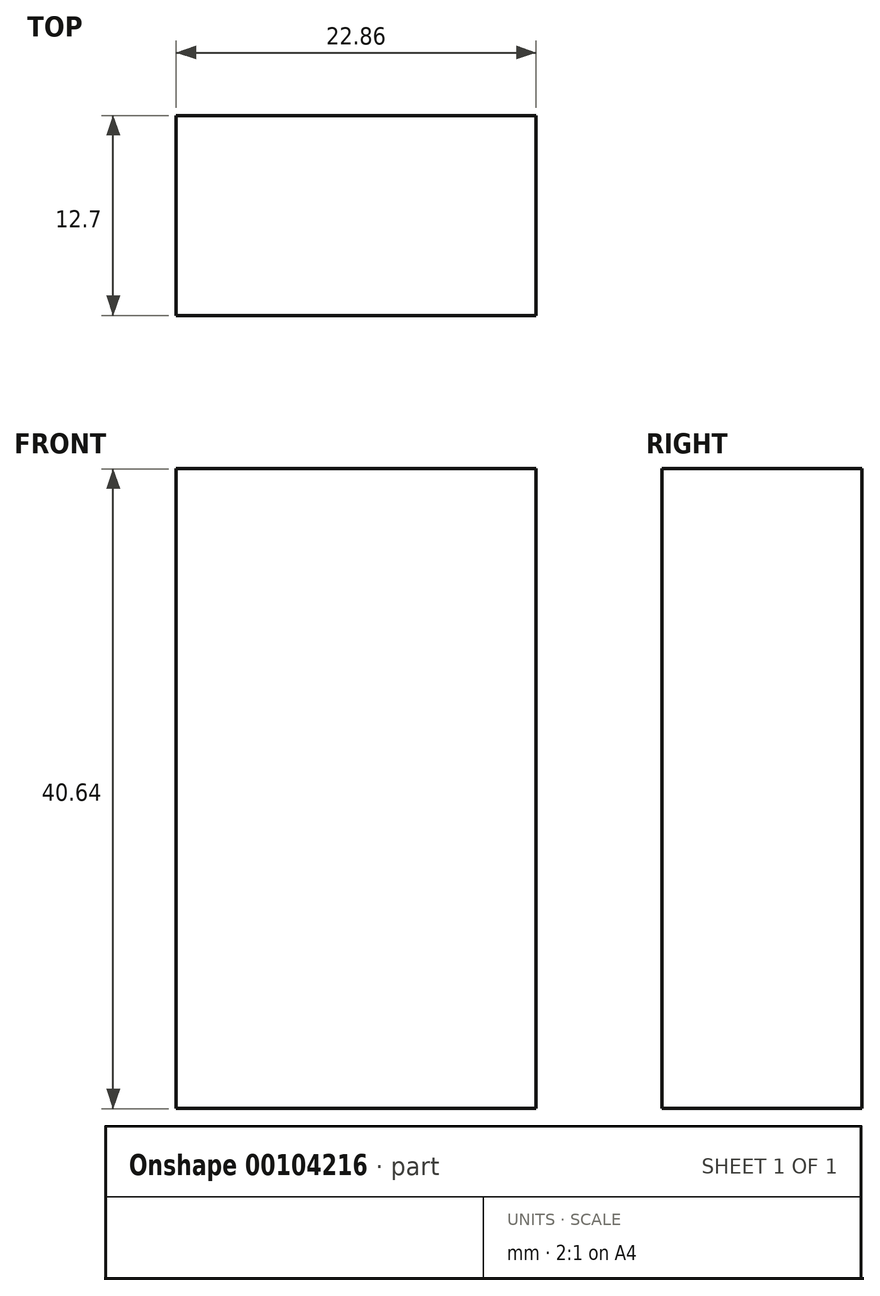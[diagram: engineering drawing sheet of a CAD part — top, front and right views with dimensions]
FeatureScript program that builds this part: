
annotation { "Feature Type Name" : "Feature", "Feature Type Description" : "" }
export const myFeature = defineFeature(function(context is Context, id is Id, definition is map)
    precondition{}
    {
        {
            var Q0;
            Q0=qCreatedBy(makeId("Front.planeOp"),FACE);
            var sketch = newSketch(context, id + "F0", { "sketchPlane" : qUnion([Q0])});
            skLineSegment(sketch, "E0.bottom", {"start": v(-20.82, -10.24) * mm, "end": v(2.04, -10.24) * mm});
            skLineSegment(sketch, "E0.top", {"start": v(-20.82, 30.4) * mm, "end": v(2.04, 30.4) * mm});
            skLineSegment(sketch, "E0.left", {"start": v(-20.82, -10.24) * mm, "end": v(-20.82, 30.4) * mm});
            skLineSegment(sketch, "E0.right", {"start": v(2.04, -10.24) * mm, "end": v(2.04, 30.4) * mm});
            skSolve(sketch);
        }
        {
            var Q0;
            Q0=makeQuery(id+"F0.imprint","IMPRINT",FACE,{"disambiguationData":[TD([[makeQuery(id+"F0.imprint","IMPRINT",EDGE,{"derivedFrom":sQuery(id+"F0.wireOp",EDGE,"E0.bottom")}),1.0]])]});
            extrude(context, id + "F1", {"entities" : qUnion([Q0]), "oppositeDirection" : true, "depth" : 12.7 * mm});
        }
    });
